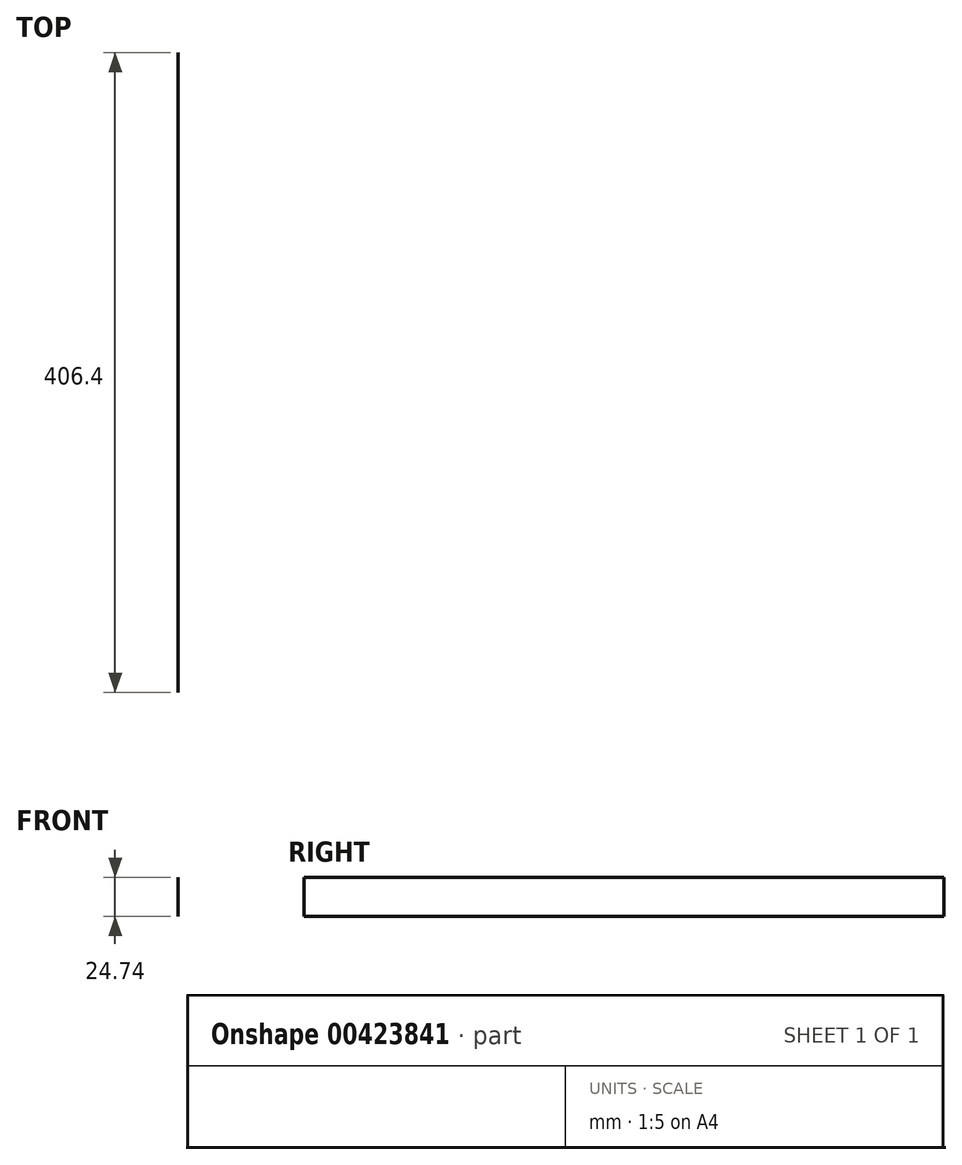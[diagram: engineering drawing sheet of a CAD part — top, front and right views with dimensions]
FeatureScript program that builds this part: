
annotation { "Feature Type Name" : "Feature", "Feature Type Description" : "" }
export const myFeature = defineFeature(function(context is Context, id is Id, definition is map)
    precondition{}
    {
        {
            var Q0;
            Q0=qCreatedBy(makeId("Front.planeOp"),FACE);
            var sketch = newSketch(context, id + "F0", { "sketchPlane" : qUnion([Q0])});
            skLineSegment(sketch, "E0.bottom", {"start": v(-6.1, 0) * mm, "end": v(0, 0) * mm});
            skLineSegment(sketch, "E0.top", {"start": v(-6.1, 24.74) * mm, "end": v(0, 24.74) * mm});
            skLineSegment(sketch, "E0.left", {"start": v(-6.1, 0) * mm, "end": v(-6.1, 24.74) * mm});
            skLineSegment(sketch, "E0.right", {"start": v(0, 0) * mm, "end": v(0, 24.74) * mm});
            skSolve(sketch);
        }
        {
            var Q0;
            Q0=sQuery(id+"F0.wireOp",EDGE,"E0.left");
            extrude(context, id + "F1", {"bodyType" : ToolBodyType.SURFACE, "surfaceEntities" : qUnion([Q0]), "depth" : 406.4 * mm});
        }
    });
